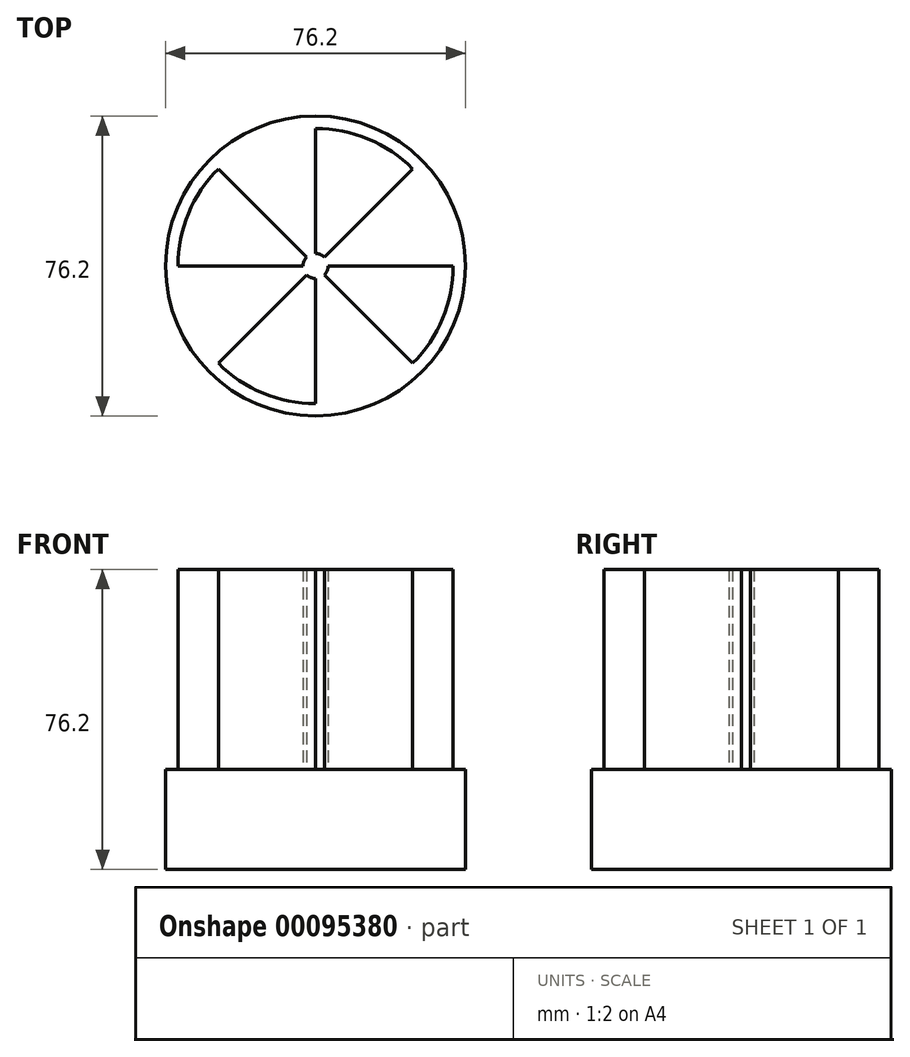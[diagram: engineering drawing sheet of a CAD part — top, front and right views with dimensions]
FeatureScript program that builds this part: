
annotation { "Feature Type Name" : "Feature", "Feature Type Description" : "" }
export const myFeature = defineFeature(function(context is Context, id is Id, definition is map)
    precondition{}
    {
        {
            var Q0;
            Q0=qCreatedBy(makeId("Top.planeOp"),FACE);
            var sketch = newSketch(context, id + "F0", { "sketchPlane" : qUnion([Q0])});
            skCircle(sketch, "E0", {"center": v(0, 0) * mm, "radius": 38.1 * mm});
            skCircle(sketch, "E1", {"center": v(0, 0) * mm, "radius": 34.93 * mm});
            skCircle(sketch, "E2", {"center": v(0, 0) * mm, "radius": 3.18 * mm});
            skLineSegment(sketch, "E3", {"start": v(0, 3.18) * mm, "end": v(0, 34.93) * mm});
            skLineSegment(sketch, "E4", {"start": v(0, -3.18) * mm, "end": v(0, -34.93) * mm});
            skLineSegment(sketch, "E5", {"start": v(3.18, 0) * mm, "end": v(34.93, 0) * mm});
            skLineSegment(sketch, "E6", {"start": v(-3.18, 0) * mm, "end": v(-34.93, 0) * mm});
            skLineSegment(sketch, "E7.1.0", {"start": v(2.25, 2.25) * mm, "end": v(24.7, 24.7) * mm});
            skLineSegment(sketch, "E7.1.1", {"start": v(-2.25, 2.25) * mm, "end": v(-24.7, 24.7) * mm});
            skLineSegment(sketch, "E7.1.2", {"start": v(-2.25, -2.25) * mm, "end": v(-24.7, -24.7) * mm});
            skLineSegment(sketch, "E7.1.3", {"start": v(2.25, -2.25) * mm, "end": v(24.7, -24.7) * mm});
            skLineSegment(sketch, "E7.anchor1", {"start": v(0, 0) * mm, "end": v(3.18, 0) * mm, "construction": true});
            skLineSegment(sketch, "E7.anchor2", {"start": v(0, 0) * mm, "end": v(2.25, 2.25) * mm, "construction": true});
            skSolve(sketch);
        }
        {
            var Q0;
            {var subQ0=sQuery(id+"F0.wireOp",EDGE,"E4");Q0=makeQuery(id+"F0.imprint","IMPRINT",FACE,{"disambiguationData":[TD([[makeQuery(id+"F0.imprint","IMPRINT",EDGE,{"derivedFrom":subQ0}),-1.0]])]});}
            var Q1;
            {var subQ0=sQuery(id+"F0.wireOp",EDGE,"E6");Q1=makeQuery(id+"F0.imprint","IMPRINT",FACE,{"disambiguationData":[TD([[makeQuery(id+"F0.imprint","IMPRINT",EDGE,{"derivedFrom":subQ0}),-1.0]])]});}
            var Q2;
            {var subQ0=sQuery(id+"F0.wireOp",EDGE,"E3");Q2=makeQuery(id+"F0.imprint","IMPRINT",FACE,{"disambiguationData":[TD([[makeQuery(id+"F0.imprint","IMPRINT",EDGE,{"derivedFrom":subQ0}),-1.0]])]});}
            var Q3;
            {var subQ0=sQuery(id+"F0.wireOp",EDGE,"E5");Q3=makeQuery(id+"F0.imprint","IMPRINT",FACE,{"disambiguationData":[TD([[makeQuery(id+"F0.imprint","IMPRINT",EDGE,{"derivedFrom":subQ0}),-1.0]])]});}
            extrude(context, id + "F1", {"entities" : qUnion([Q0, Q1, Q2, Q3]), "depth" : 50.8 * mm});
        }
        {
            var Q0;
            Q0=qCreatedBy(makeId("Top.planeOp"),FACE);
            var sketch = newSketch(context, id + "F2", { "sketchPlane" : qUnion([Q0])});
            skCircle(sketch, "E8", {"center": v(0, 0) * mm, "radius": 38.1 * mm});
            skSolve(sketch);
        }
        {
            var Q0;
            Q0 = qSketchRegion(id + "F2", true);
            extrude(context, id + "F3", {"entities" : qUnion([Q0]), "oppositeDirection" : true, "depth" : 25.4 * mm});
        }
    });
